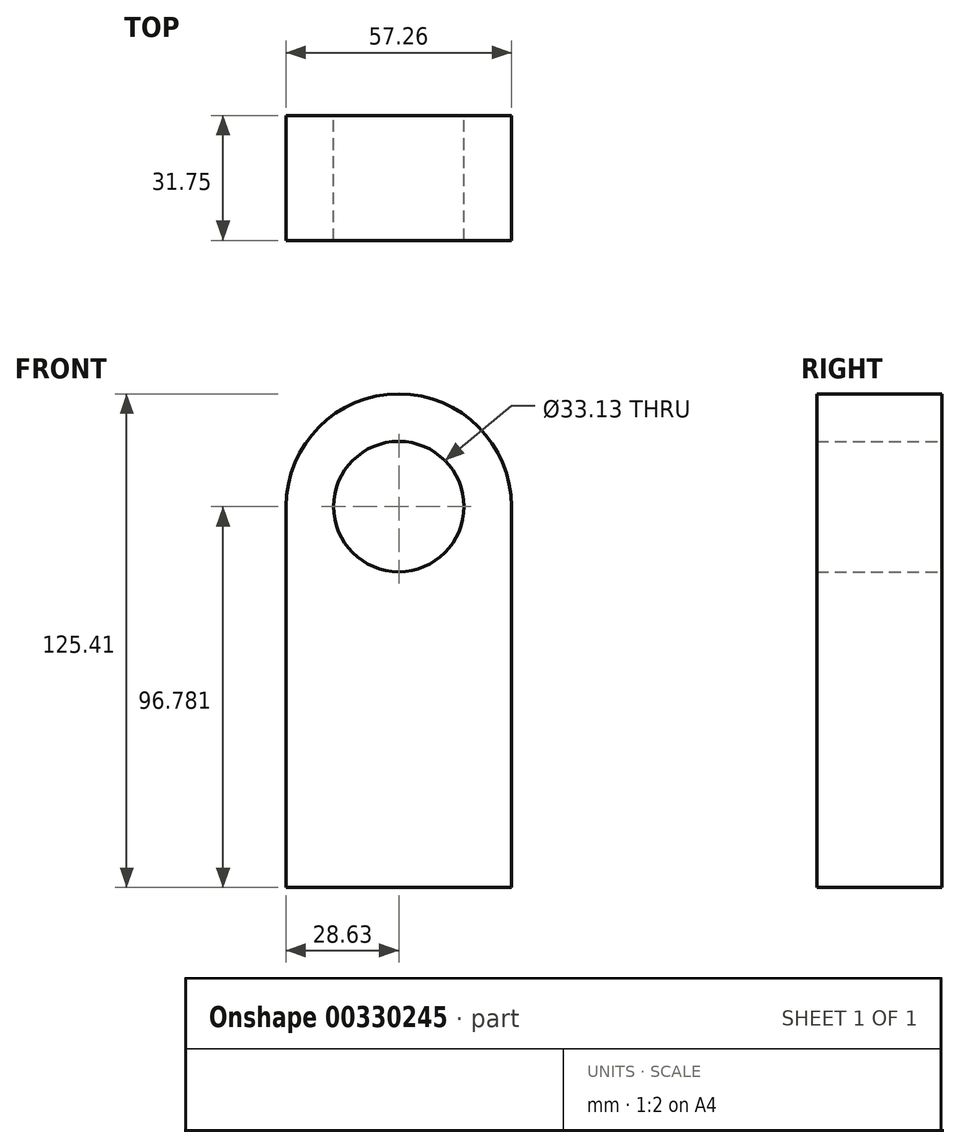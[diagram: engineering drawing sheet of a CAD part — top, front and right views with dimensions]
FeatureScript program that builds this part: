
annotation { "Feature Type Name" : "Feature", "Feature Type Description" : "" }
export const myFeature = defineFeature(function(context is Context, id is Id, definition is map)
    precondition{}
    {
        {
            var Q0;
            Q0=qCreatedBy(makeId("Front.planeOp"),FACE);
            var sketch = newSketch(context, id + "F0", { "sketchPlane" : qUnion([Q0])});
            skLineSegment(sketch, "E0.bottom", {"start": v(28.63, -48.4) * mm, "end": v(-28.63, -48.4) * mm});
            skLineSegment(sketch, "E0.left", {"start": v(28.63, -48.4) * mm, "end": v(28.63, 48.4) * mm});
            skLineSegment(sketch, "E0.right", {"start": v(-28.63, -48.4) * mm, "end": v(-28.63, 48.4) * mm});
            skPoint(sketch, "E0.middle", {"position": v(0, 0) * mm});
            skArc(sketch, "E1", {"start": v(-28.63, 48.4) * mm, "mid": v(0, 77.02) * mm, "end": v(28.63, 48.4) * mm});
            skCircle(sketch, "E2", {"center": v(0, 48.4) * mm, "radius": 16.56 * mm});
            skSolve(sketch);
        }
        {
            var Q0;
            Q0=makeQuery(id+"F0.imprint","IMPRINT",FACE,{"disambiguationData":[TD([[makeQuery(id+"F0.imprint","IMPRINT",EDGE,{"derivedFrom":sQuery(id+"F0.wireOp",EDGE,"E0.bottom")}),-1.0]])]});
            extrude(context, id + "F1", {"entities" : qUnion([Q0]), "depth" : 31.75 * mm});
        }
    });
